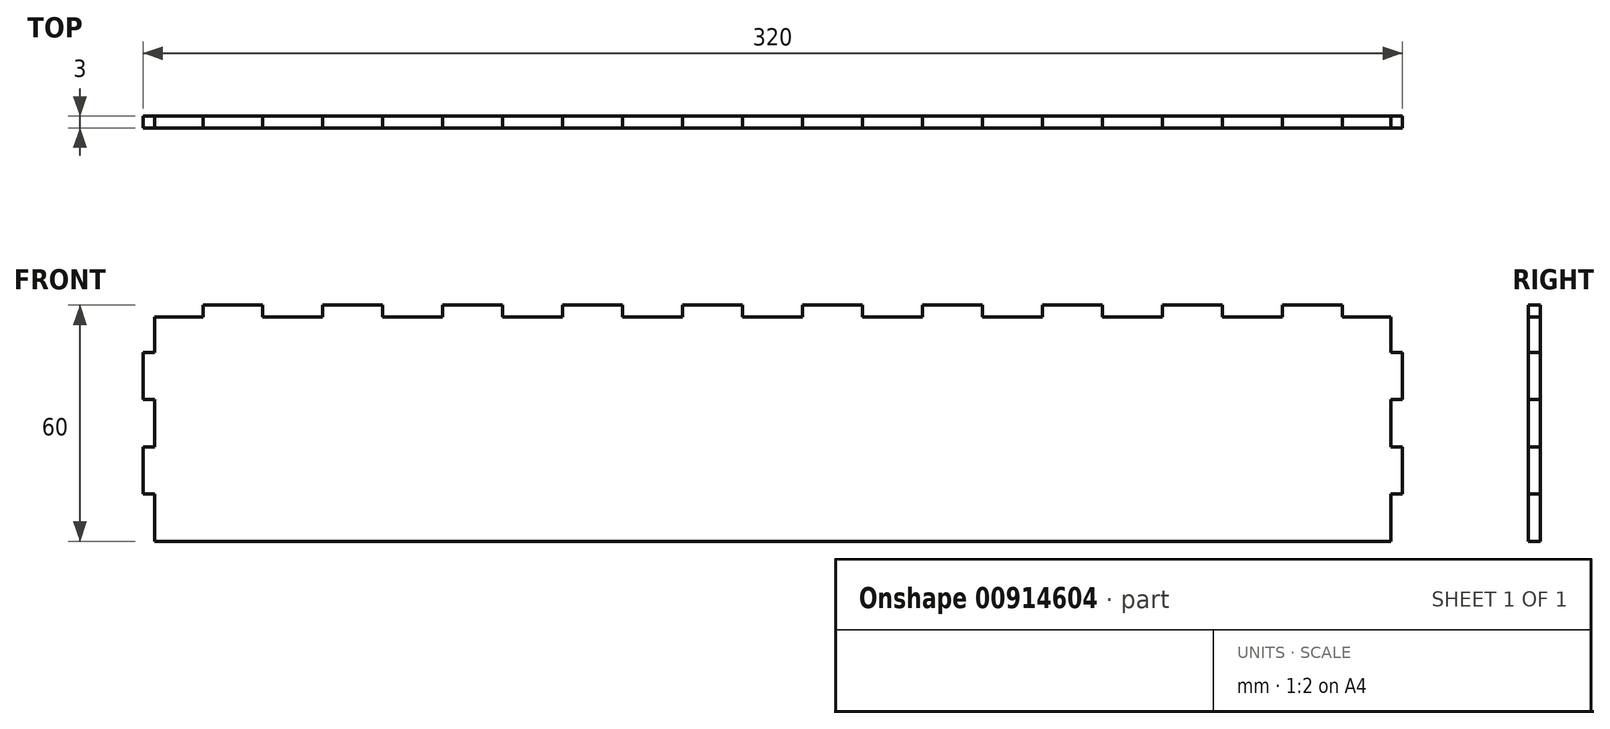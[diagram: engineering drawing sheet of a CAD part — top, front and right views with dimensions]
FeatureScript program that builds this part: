
annotation { "Feature Type Name" : "Feature", "Feature Type Description" : "" }
export const myFeature = defineFeature(function(context is Context, id is Id, definition is map)
    precondition{}
    {
        {
            var Q0;
            Q0=qCreatedBy(makeId("Front.planeOp"),FACE);
            var sketch = newSketch(context, id + "F0", { "sketchPlane" : qUnion([Q0])});
            skLineSegment(sketch, "E0.bottom", {"start": v(157, -30) * mm, "end": v(-157, -30) * mm});
            skLineSegment(sketch, "E0.top", {"start": v(144.76, 30) * mm, "end": v(129.52, 30) * mm});
            skLineSegment(sketch, "E0.right", {"start": v(-160, -18) * mm, "end": v(-160, -6) * mm});
            skPoint(sketch, "E0.middle", {"position": v(0, 0) * mm});
            skLineSegment(sketch, "E1", {"start": v(-157, 27) * mm, "end": v(-144.76, 27) * mm});
            skLineSegment(sketch, "E2", {"start": v(-99.05, 30) * mm, "end": v(-99.05, 27) * mm});
            skLineSegment(sketch, "E3", {"start": v(-83.8, 30) * mm, "end": v(-83.8, 27) * mm});
            skLineSegment(sketch, "E4", {"start": v(-53.33, 30) * mm, "end": v(-53.33, 27) * mm});
            skLineSegment(sketch, "E5", {"start": v(-22.86, 30) * mm, "end": v(-22.86, 27) * mm});
            skLineSegment(sketch, "E6", {"start": v(-144.76, 30) * mm, "end": v(-144.76, 27) * mm});
            skLineSegment(sketch, "E7", {"start": v(-129.52, 30) * mm, "end": v(-129.52, 27) * mm});
            skLineSegment(sketch, "E8", {"start": v(-114.29, 30) * mm, "end": v(-114.29, 27) * mm});
            skLineSegment(sketch, "E9", {"start": v(-68.57, 30) * mm, "end": v(-68.57, 27) * mm});
            skLineSegment(sketch, "E10", {"start": v(-38.1, 30) * mm, "end": v(-38.1, 27) * mm});
            skLineSegment(sketch, "E11", {"start": v(-7.62, 30) * mm, "end": v(-7.62, 27) * mm});
            skLineSegment(sketch, "E12", {"start": v(7.62, 30) * mm, "end": v(7.62, 27) * mm});
            skLineSegment(sketch, "E13", {"start": v(22.86, 30) * mm, "end": v(22.86, 27) * mm});
            skLineSegment(sketch, "E14", {"start": v(38.1, 30) * mm, "end": v(38.1, 27) * mm});
            skLineSegment(sketch, "E15", {"start": v(53.33, 30) * mm, "end": v(53.33, 27) * mm});
            skLineSegment(sketch, "E16", {"start": v(68.57, 30) * mm, "end": v(68.57, 27) * mm});
            skLineSegment(sketch, "E17", {"start": v(83.8, 30) * mm, "end": v(83.8, 27) * mm});
            skLineSegment(sketch, "E18", {"start": v(99.05, 30) * mm, "end": v(99.05, 27) * mm});
            skLineSegment(sketch, "E19", {"start": v(114.29, 30) * mm, "end": v(114.29, 27) * mm});
            skLineSegment(sketch, "E20", {"start": v(129.52, 30) * mm, "end": v(129.52, 27) * mm});
            skLineSegment(sketch, "E21", {"start": v(144.76, 30) * mm, "end": v(144.76, 27) * mm});
            skLineSegment(sketch, "E22.trimOffspring", {"start": v(144.76, 27) * mm, "end": v(157, 27) * mm});
            skLineSegment(sketch, "E23.trimOffspring", {"start": v(114.29, 30) * mm, "end": v(99.05, 30) * mm});
            skLineSegment(sketch, "E24.trimOffspring", {"start": v(114.29, 27) * mm, "end": v(129.52, 27) * mm});
            skLineSegment(sketch, "E25.trimOffspring", {"start": v(83.8, 30) * mm, "end": v(68.57, 30) * mm});
            skLineSegment(sketch, "E26.trimOffspring", {"start": v(83.8, 27) * mm, "end": v(99.05, 27) * mm});
            skLineSegment(sketch, "E27.trimOffspring", {"start": v(53.33, 30) * mm, "end": v(38.1, 30) * mm});
            skLineSegment(sketch, "E28.trimOffspring", {"start": v(53.33, 27) * mm, "end": v(68.57, 27) * mm});
            skLineSegment(sketch, "E29.trimOffspring", {"start": v(22.86, 30) * mm, "end": v(7.62, 30) * mm});
            skLineSegment(sketch, "E30.trimOffspring", {"start": v(22.86, 27) * mm, "end": v(38.1, 27) * mm});
            skLineSegment(sketch, "E31.trimOffspring", {"start": v(-7.62, 30) * mm, "end": v(-22.86, 30) * mm});
            skLineSegment(sketch, "E32.trimOffspring", {"start": v(-7.62, 27) * mm, "end": v(7.62, 27) * mm});
            skLineSegment(sketch, "E33.trimOffspring", {"start": v(-38.1, 30) * mm, "end": v(-53.33, 30) * mm});
            skLineSegment(sketch, "E34.trimOffspring", {"start": v(-38.1, 27) * mm, "end": v(-22.86, 27) * mm});
            skLineSegment(sketch, "E35.trimOffspring", {"start": v(-68.57, 30) * mm, "end": v(-83.8, 30) * mm});
            skLineSegment(sketch, "E36.trimOffspring", {"start": v(-68.57, 27) * mm, "end": v(-53.33, 27) * mm});
            skLineSegment(sketch, "E37.trimOffspring", {"start": v(-99.05, 30) * mm, "end": v(-114.29, 30) * mm});
            skLineSegment(sketch, "E38.trimOffspring", {"start": v(-99.05, 27) * mm, "end": v(-83.8, 27) * mm});
            skLineSegment(sketch, "E39.trimOffspring", {"start": v(-129.52, 30) * mm, "end": v(-144.76, 30) * mm});
            skLineSegment(sketch, "E40.trimOffspring", {"start": v(-129.52, 27) * mm, "end": v(-114.29, 27) * mm});
            skPoint(sketch, "E41.orphan", {"position": v(-160, 30) * mm});
            skPoint(sketch, "E42.orphan", {"position": v(160, 30) * mm});
            skLineSegment(sketch, "E43", {"start": v(-157, -30) * mm, "end": v(-157, -18) * mm});
            skLineSegment(sketch, "E44", {"start": v(-160, 18) * mm, "end": v(-157, 18) * mm});
            skLineSegment(sketch, "E45", {"start": v(-160, 6) * mm, "end": v(-157, 6) * mm});
            skLineSegment(sketch, "E46", {"start": v(-160, -6) * mm, "end": v(-157, -6) * mm});
            skLineSegment(sketch, "E47", {"start": v(-160, -18) * mm, "end": v(-157, -18) * mm});
            skLineSegment(sketch, "E48.trimOffspring", {"start": v(-157, 18) * mm, "end": v(-157, 27) * mm});
            skLineSegment(sketch, "E49.trimOffspring", {"start": v(-160, 6) * mm, "end": v(-160, 18) * mm});
            skLineSegment(sketch, "E50.trimOffspring", {"start": v(-157, -6) * mm, "end": v(-157, 6) * mm});
            skPoint(sketch, "E51.orphan", {"position": v(-160, -30) * mm});
            skLineSegment(sketch, "E52.MirrorCS", {"start": v(160, 6) * mm, "end": v(157, 6) * mm});
            skLineSegment(sketch, "E53.MirrorCS", {"start": v(160, -18) * mm, "end": v(157, -18) * mm});
            skLineSegment(sketch, "E54.MirrorCS", {"start": v(160, -6) * mm, "end": v(157, -6) * mm});
            skLineSegment(sketch, "E55.MirrorCS", {"start": v(160, 18) * mm, "end": v(157, 18) * mm});
            skLineSegment(sketch, "E56.MirrorCS", {"start": v(160, 6) * mm, "end": v(160, 18) * mm});
            skLineSegment(sketch, "E57.MirrorCS", {"start": v(160, -18) * mm, "end": v(160, -6) * mm});
            skLineSegment(sketch, "E58.MirrorCS", {"start": v(157, 18) * mm, "end": v(157, 27) * mm});
            skLineSegment(sketch, "E59.MirrorCS", {"start": v(157, -30) * mm, "end": v(157, -18) * mm});
            skLineSegment(sketch, "E60.MirrorCS", {"start": v(157, -6) * mm, "end": v(157, 6) * mm});
            skPoint(sketch, "E61.MirrorP", {"position": v(160, -30) * mm});
            skSolve(sketch);
        }
        {
            var Q0;
            Q0=makeQuery(id+"F0.imprint","IMPRINT",FACE,{"disambiguationData":[TD([[makeQuery(id+"F0.imprint","IMPRINT",EDGE,{"derivedFrom":sQuery(id+"F0.wireOp",EDGE,"E0.bottom")}),-1.0]])]});
            extrude(context, id + "F1", {"entities" : qUnion([Q0]), "depth" : 3 * mm, "offsetDistance" : 25 * mm});
        }
    });
